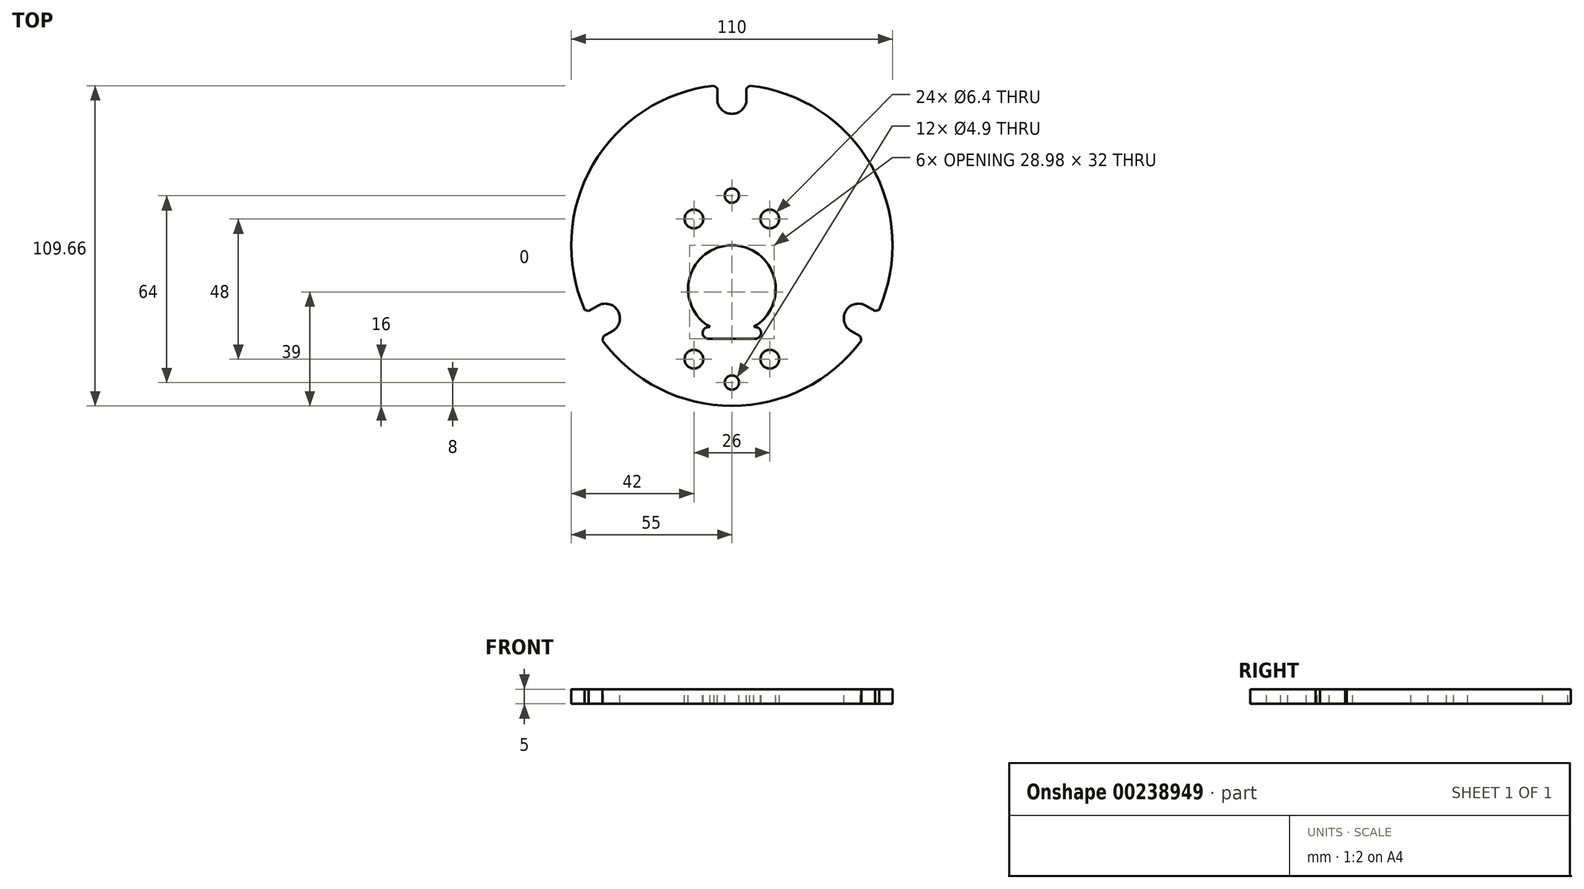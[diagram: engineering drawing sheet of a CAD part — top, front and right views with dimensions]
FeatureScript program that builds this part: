
annotation { "Feature Type Name" : "Feature", "Feature Type Description" : "" }
export const myFeature = defineFeature(function(context is Context, id is Id, definition is map)
    precondition{}
    {
        {
            var Q0;
            Q0=qCreatedBy(makeId("Top.planeOp"),FACE);
            var sketch = newSketch(context, id + "F0", { "sketchPlane" : qUnion([Q0])});
            skCircle(sketch, "E0", {"center": v(0, 0) * mm, "radius": 95 * mm, "construction": true});
            skPoint(sketch, "E1", {"position": v(0, -15) * mm});
            skPoint(sketch, "E2", {"position": v(0, 15) * mm});
            skCircle(sketch, "E3", {"center": v(0, 15) * mm, "radius": 80 * mm, "construction": true});
            skCircle(sketch, "E4", {"center": v(0, 15) * mm, "radius": 70 * mm, "construction": true});
            skLineSegment(sketch, "E5", {"start": v(0, 15) * mm, "end": v(-99.15, 72.25) * mm, "construction": true});
            skLineSegment(sketch, "E6.MirrorCS", {"start": v(0, 15) * mm, "end": v(99.15, 72.25) * mm, "construction": true});
            skArc(sketch, "E7.1.0", {"start": v(40.59, 44.2) * mm, "mid": v(7.54, 64.43) * mm, "end": v(-30.04, 54.97) * mm, "construction": true});
            skArc(sketch, "E8.trimOffspring", {"start": v(50.4, -7.04) * mm, "mid": v(47.63, 42.5) * mm, "end": v(6.11, 69.66) * mm});
            skArc(sketch, "E9.trimOffspring", {"start": v(-46.91, 32.3) * mm, "mid": v(1.75, -34.97) * mm, "end": v(45.58, 35.55) * mm, "construction": true});
            skCircle(sketch, "E10", {"center": v(0, 0) * mm, "radius": 15 * mm});
            skArc(sketch, "E11", {"start": v(-5, 65) * mm, "mid": v(0, 60) * mm, "end": v(5, 65) * mm});
            skLineSegment(sketch, "E12", {"start": v(5, 68.67) * mm, "end": v(5, 64.75) * mm});
            skLineSegment(sketch, "E13", {"start": v(-5, 68.67) * mm, "end": v(-5, 64.75) * mm});
            skArc(sketch, "E14.trimOffspring", {"start": v(-6.11, 69.66) * mm, "mid": v(-47.36, 42.97) * mm, "end": v(-50.82, -6.03) * mm});
            skLineSegment(sketch, "E15", {"start": v(-6.11, 69.66) * mm, "end": v(-5, 68.67) * mm});
            skLineSegment(sketch, "E16", {"start": v(6.11, 69.66) * mm, "end": v(5, 68.67) * mm});
            skCircle(sketch, "E17", {"center": v(0, 65) * mm, "radius": 5 * mm, "construction": true});
            skCircle(sketch, "E18", {"center": v(0, 65) * mm, "radius": 8.5 * mm, "construction": true});
            skCircle(sketch, "E19", {"center": v(0, 65) * mm, "radius": 20 * mm, "construction": true});
            skCircle(sketch, "E20.1.0", {"center": v(-43.3, -10) * mm, "radius": 8.5 * mm, "construction": true});
            skPoint(sketch, "E20.1.1", {"position": v(-43.3, -10) * mm});
            skCircle(sketch, "E20.1.2", {"center": v(-43.3, -10) * mm, "radius": 5 * mm, "construction": true});
            skLineSegment(sketch, "E20.1.3", {"start": v(-43.98, -16.16) * mm, "end": v(-40.58, -14.2) * mm});
            skArc(sketch, "E20.1.4", {"start": v(-40.8, -14.33) * mm, "mid": v(-38.97, -7.5) * mm, "end": v(-45.8, -5.67) * mm});
            skLineSegment(sketch, "E20.1.5", {"start": v(-44.28, -17.62) * mm, "end": v(-43.98, -16.16) * mm});
            skLineSegment(sketch, "E20.1.6", {"start": v(-48.98, -7.5) * mm, "end": v(-45.58, -5.54) * mm});
            skLineSegment(sketch, "E20.1.7", {"start": v(-50.4, -7.04) * mm, "end": v(-48.98, -7.5) * mm});
            skCircle(sketch, "E20.1.8", {"center": v(-43.3, -10) * mm, "radius": 20 * mm, "construction": true});
            skCircle(sketch, "E20.2.0", {"center": v(43.3, -10) * mm, "radius": 8.5 * mm, "construction": true});
            skPoint(sketch, "E20.2.1", {"position": v(43.3, -10) * mm});
            skCircle(sketch, "E20.2.2", {"center": v(43.3, -10) * mm, "radius": 5 * mm, "construction": true});
            skLineSegment(sketch, "E20.2.3", {"start": v(48.98, -7.5) * mm, "end": v(45.58, -5.54) * mm});
            skArc(sketch, "E20.2.4", {"start": v(45.8, -5.67) * mm, "mid": v(38.97, -7.5) * mm, "end": v(40.8, -14.33) * mm});
            skLineSegment(sketch, "E20.2.5", {"start": v(50.4, -7.04) * mm, "end": v(48.98, -7.5) * mm});
            skLineSegment(sketch, "E20.2.6", {"start": v(43.98, -16.16) * mm, "end": v(40.58, -14.2) * mm});
            skLineSegment(sketch, "E20.2.7", {"start": v(44.28, -17.62) * mm, "end": v(43.98, -16.16) * mm});
            skCircle(sketch, "E20.2.8", {"center": v(43.3, -10) * mm, "radius": 20 * mm, "construction": true});
            skArc(sketch, "E21.trimOffspring", {"start": v(-50.82, -6.03) * mm, "mid": v(-50.6, -6.54) * mm, "end": v(-50.4, -7.04) * mm});
            skArc(sketch, "E22.trimOffspring", {"start": v(-44.28, -17.62) * mm, "mid": v(0, -40) * mm, "end": v(44.28, -17.62) * mm});
            skCircle(sketch, "E23", {"center": v(0, 0) * mm, "radius": 55 * mm, "construction": true});
            skCircle(sketch, "E24", {"center": v(0, 0) * mm, "radius": 40 * mm, "construction": true});
            skCircle(sketch, "E25", {"center": v(0, 0) * mm, "radius": 33.5 * mm, "construction": true});
            skLineSegment(sketch, "E26", {"start": v(-13, 12.1) * mm, "end": v(-13, -37.02) * mm, "construction": true});
            skLineSegment(sketch, "E27", {"start": v(-31.23, -24) * mm, "end": v(-2.5, -24) * mm, "construction": true});
            skLineSegment(sketch, "E28", {"start": v(-31.23, -32) * mm, "end": v(8.76, -32) * mm, "construction": true});
            skCircle(sketch, "E29", {"center": v(-13, -24) * mm, "radius": 3.2 * mm});
            skCircle(sketch, "E30", {"center": v(0, -32) * mm, "radius": 2.45 * mm});
            skCircle(sketch, "E31.MirrorC", {"center": v(13, -24) * mm, "radius": 3.2 * mm});
            skCircle(sketch, "E32.MirrorC", {"center": v(-13, 24) * mm, "radius": 3.2 * mm});
            skCircle(sketch, "E33.MirrorC", {"center": v(13, 24) * mm, "radius": 3.2 * mm});
            skCircle(sketch, "E34.MirrorC", {"center": v(0, 32) * mm, "radius": 2.45 * mm});
            skCircle(sketch, "E35", {"center": v(0, 0) * mm, "radius": 12.5 * mm, "construction": true});
            skSolve(sketch);
        }
        {
            var Q0;
            Q0=qSketchRegion(id+"F0",true);
            extrude(context, id + "F1", {"entities" : qUnion([Q0]), "oppositeDirection" : true, "depth" : 12 * mm, "hasSecondDirection" : true, "secondDirectionOppositeDirection" : true, "secondDirectionDepth" : 7 * mm});
        }
        {
            var Q0;
            Q0=qCreatedBy(makeId("Top.planeOp"),FACE);
            var sketch = newSketch(context, id + "F2", { "sketchPlane" : qUnion([Q0])});
            skCircle(sketch, "E36.0", {"center": v(0, 0) * mm, "radius": 12.5 * mm, "construction": true});
            skLineSegment(sketch, "E37", {"start": v(-12.89, -12.5) * mm, "end": v(0, -12.5) * mm, "construction": true});
            skLineSegment(sketch, "E38", {"start": v(-8, -13) * mm, "end": v(0, -13) * mm});
            skLineSegment(sketch, "E39", {"start": v(-8, -8.9) * mm, "end": v(-8, -21.1) * mm, "construction": true});
            skArc(sketch, "E40", {"start": v(-8, -13) * mm, "mid": v(-10, -15) * mm, "end": v(-8, -17) * mm});
            skLineSegment(sketch, "E41", {"start": v(-8, -17) * mm, "end": v(0, -17) * mm});
            skPoint(sketch, "E42.orphan", {"position": v(0, -5.52) * mm});
            skLineSegment(sketch, "E43.MirrorCS", {"start": v(8, -13) * mm, "end": v(0, -13) * mm});
            skArc(sketch, "E44.MirrorCS", {"start": v(8, -13) * mm, "mid": v(10, -15) * mm, "end": v(8, -17) * mm});
            skLineSegment(sketch, "E45.MirrorCS", {"start": v(8, -17) * mm, "end": v(0, -17) * mm});
            skCircle(sketch, "E46.0", {"center": v(0, 0) * mm, "radius": 15 * mm, "construction": true});
            skSolve(sketch);
        }
        {
            var Q0;
            Q0=qSketchRegion(id+"F2",true);
            extrude(context, id + "F3", {"entities" : qUnion([Q0]), "operationType" : NewBodyOperationType.REMOVE, "oppositeDirection" : true, "depth" : 40 * mm, "hasSecondDirection" : true, "secondDirectionOppositeDirection" : false, "secondDirectionDepth" : 40 * mm});
        }
    });
